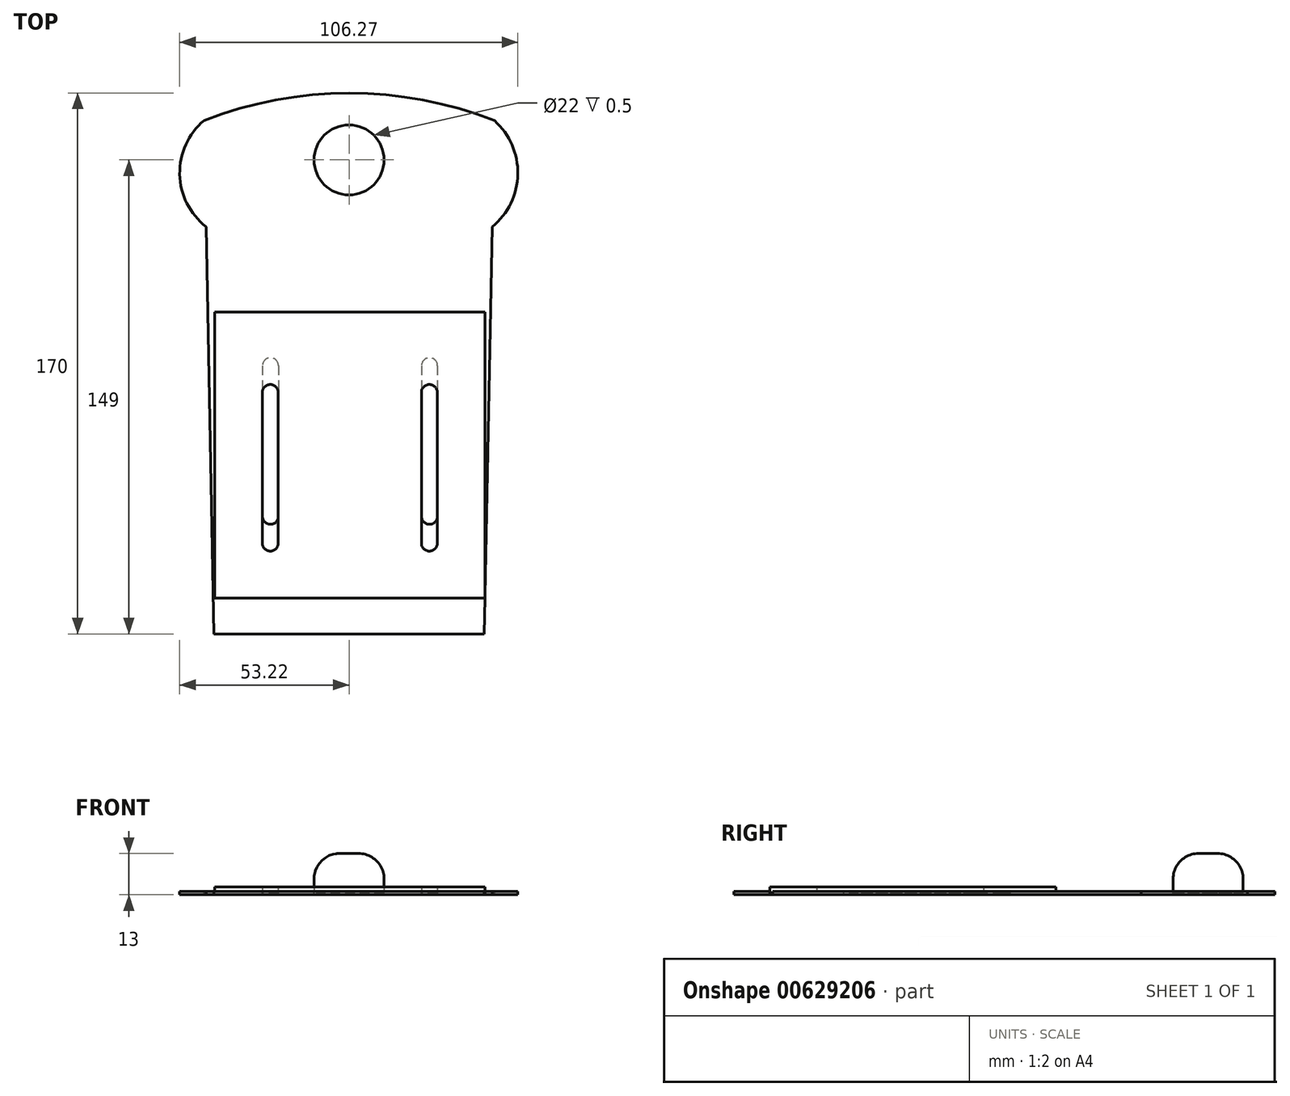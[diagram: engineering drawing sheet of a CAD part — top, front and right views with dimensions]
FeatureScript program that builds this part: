
annotation { "Feature Type Name" : "Feature", "Feature Type Description" : "" }
export const myFeature = defineFeature(function(context is Context, id is Id, definition is map)
    precondition{}
    {
        {
            var Q0;
            Q0=qCreatedBy(makeId("Top.planeOp"),FACE);
            var sketch = newSketch(context, id + "F0", { "sketchPlane" : qUnion([Q0])});
            skCircle(sketch, "E0", {"center": v(0, 0) * mm, "radius": 125 * mm});
            skCircle(sketch, "E1", {"center": v(0, 104) * mm, "radius": 11 * mm});
            skLineSegment(sketch, "E2", {"start": v(-45.58, 116.4) * mm, "end": v(-42.5, -45) * mm});
            skLineSegment(sketch, "E3", {"start": v(-42.5, -45) * mm, "end": v(42.5, -45) * mm});
            skLineSegment(sketch, "E4", {"start": v(45.72, 116.34) * mm, "end": v(42.5, -45) * mm});
            skLineSegment(sketch, "E5", {"start": v(0, 104) * mm, "end": v(0, 115) * mm});
            skLineSegment(sketch, "E6", {"start": v(-44.94, 83) * mm, "end": v(45.06, 83) * mm});
            skCircle(sketch, "E7", {"center": v(-31.72, 99.95) * mm, "radius": 21.5 * mm});
            skCircle(sketch, "E8", {"center": v(31.07, 99.95) * mm, "radius": 21.98 * mm});
            skLineSegment(sketch, "E9.bottom", {"start": v(-42.2, -34.93) * mm, "end": v(42.8, -34.93) * mm});
            skLineSegment(sketch, "E9.top", {"start": v(-42.2, 55.07) * mm, "end": v(42.8, 55.07) * mm});
            skLineSegment(sketch, "E9.left", {"start": v(-42.2, -34.93) * mm, "end": v(-42.2, 55.07) * mm});
            skLineSegment(sketch, "E9.right", {"start": v(42.8, -34.93) * mm, "end": v(42.8, 55.07) * mm});
            skLineSegment(sketch, "E10", {"start": v(-22.2, 39.32) * mm, "end": v(-22.2, -8.05) * mm});
            skLineSegment(sketch, "E11", {"start": v(22.8, 39.32) * mm, "end": v(22.8, -8.05) * mm});
            skLineSegment(sketch, "E12", {"start": v(-27.2, 39.32) * mm, "end": v(-27.2, -8.05) * mm});
            skLineSegment(sketch, "E13", {"start": v(27.8, 39.32) * mm, "end": v(27.8, -8.05) * mm});
            skCircle(sketch, "E14", {"center": v(-24.7, 39.32) * mm, "radius": 2.5 * mm});
            skCircle(sketch, "E15", {"center": v(-24.7, -8.05) * mm, "radius": 2.5 * mm});
            skCircle(sketch, "E16", {"center": v(25.3, -8.05) * mm, "radius": 2.5 * mm});
            skCircle(sketch, "E17", {"center": v(25.3, 39.32) * mm, "radius": 2.5 * mm});
            skSolve(sketch);
        }
        {
            var Q0;
            Q0=makeQuery(id+"F0.imprint","IMPRINT",FACE,{"disambiguationData":[TD([[makeQuery(id+"F0.imprint","IMPRINT",EDGE,{"derivedFrom":sQuery(id+"F0.wireOp",EDGE,"E1")}),1.0]])]});
            var Q1;
            {var subQ0=sQuery(id+"F0.wireOp",EDGE,"E8");var subQ1=sQuery(id+"F0.wireOp",EDGE,"E1");var subQ2=makeQuery(id+"F0.imprint","INTERSECT",VERTEX,{"disambiguationData":[OD(0.0)],"derivedFrom":[subQ1,subQ0]});Q1=makeQuery(id+"F0.imprint","IMPRINT",FACE,{"disambiguationData":[TD([[makeQuery(id+"F0.imprint","IMPRINT",EDGE,{"disambiguationData":[TD([[subQ2,1.0]])],"derivedFrom":subQ1}),1.0]])]});}
            var Q2;
            {var subQ0=sQuery(id+"F0.wireOp",EDGE,"E7");var subQ1=sQuery(id+"F0.wireOp",EDGE,"E1");var subQ2=makeQuery(id+"F0.imprint","INTERSECT",VERTEX,{"disambiguationData":[OD(0.0)],"derivedFrom":[subQ1,subQ0]});Q2=makeQuery(id+"F0.imprint","IMPRINT",FACE,{"disambiguationData":[TD([[makeQuery(id+"F0.imprint","IMPRINT",EDGE,{"disambiguationData":[TD([[subQ2,-1.0]])],"derivedFrom":subQ1}),1.0]])]});}
            extrude(context, id + "F1", {"entities" : qUnion([Q0, Q1, Q2]), "depth" : 12.5 * mm, "offsetDistance" : 25 * mm});
        }
        {
            var Q0;
            Q0=makeQuery(id+"F1.opExtrude","CAP_EDGE",EDGE,{"disambiguationData":[OSD([sQuery(id+"F0.wireOp",EDGE,"E1")])],"isStart":false});
            fillet(context, id + "F2", {"entities" : qUnion([Q0]), "radius" : 8 * mm, "tangentPropagation" : true, "allowEdgeOverflow" : false});
        }
        {
            var Q0;
            {var subQ0=sQuery(id+"F0.wireOp",EDGE,"E3");Q0=makeQuery(id+"F0.imprint","IMPRINT",FACE,{"disambiguationData":[TD([[makeQuery(id+"F0.imprint","IMPRINT",EDGE,{"derivedFrom":subQ0}),-1.0]])]});}
            var sketch = newSketch(context, id + "F3", { "sketchPlane" : qUnion([Q0])});
            skLineSegment(sketch, "E18.bottom", {"start": v(-42.26, -33.76) * mm, "end": v(42.74, -33.76) * mm});
            skLineSegment(sketch, "E18.top", {"start": v(-42.26, 56.24) * mm, "end": v(42.74, 56.24) * mm});
            skLineSegment(sketch, "E18.left", {"start": v(-42.26, -33.76) * mm, "end": v(-42.26, 56.24) * mm});
            skLineSegment(sketch, "E18.right", {"start": v(42.74, -33.76) * mm, "end": v(42.74, 56.24) * mm});
            skLineSegment(sketch, "E19", {"start": v(-22.26, 30.9) * mm, "end": v(-22.26, -16.47) * mm});
            skLineSegment(sketch, "E20", {"start": v(22.74, 30.9) * mm, "end": v(22.74, -16.47) * mm});
            skLineSegment(sketch, "E21", {"start": v(-27.26, 30.9) * mm, "end": v(-27.26, -16.47) * mm});
            skLineSegment(sketch, "E22", {"start": v(27.74, 30.9) * mm, "end": v(27.74, -16.47) * mm});
            skCircle(sketch, "E23", {"center": v(-24.76, 30.9) * mm, "radius": 2.5 * mm});
            skCircle(sketch, "E24", {"center": v(-24.76, -16.47) * mm, "radius": 2.5 * mm});
            skCircle(sketch, "E25", {"center": v(25.24, -16.47) * mm, "radius": 2.5 * mm});
            skCircle(sketch, "E26", {"center": v(25.24, 30.9) * mm, "radius": 2.5 * mm});
            skSolve(sketch);
        }
        {
            var Q0;
            {var subQ11=sQuery(id+"F3.wireOp",EDGE,"E18.top");Q0=makeQuery(id+"F3.imprint","IMPRINT",FACE,{"disambiguationData":[TD([[makeQuery(id+"F3.imprint","IMPRINT",EDGE,{"derivedFrom":subQ11}),-1.0]])]});}
            extrude(context, id + "F4", {"entities" : qUnion([Q0]), "depth" : 2 * mm, "offsetDistance" : 25 * mm});
        }
        {
            var Q0;
            {var subQ0=sQuery(id+"F0.wireOp",EDGE,"E8");var subQ7=sQuery(id+"F0.wireOp",EDGE,"E1");var subQ8=makeQuery(id+"F0.imprint","INTERSECT",VERTEX,{"disambiguationData":[OD(0.0)],"derivedFrom":[subQ7,subQ0]});Q0=makeQuery(id+"F0.imprint","IMPRINT",FACE,{"disambiguationData":[TD([[makeQuery(id+"F0.imprint","IMPRINT",EDGE,{"disambiguationData":[TD([[subQ8,1.0]])],"derivedFrom":subQ7}),-1.0]])]});}
            var Q1;
            {var subQ0=sQuery(id+"F0.wireOp",EDGE,"E8");var subQ1=sQuery(id+"F0.wireOp",EDGE,"E4");var subQ2=makeQuery(id+"F0.imprint","INTERSECT",VERTEX,{"derivedFrom":[sQuery(id+"F0.wireOp",EDGE,"E0"),subQ1,subQ0]});Q1=makeQuery(id+"F0.imprint","IMPRINT",FACE,{"disambiguationData":[TD([[makeQuery(id+"F0.imprint","IMPRINT",EDGE,{"disambiguationData":[TD([[subQ2,-1.0]])],"derivedFrom":subQ1}),1.0]])]});}
            var Q2;
            {var subQ0=sQuery(id+"F0.wireOp",EDGE,"E8");var subQ1=sQuery(id+"F0.wireOp",EDGE,"E6");var subQ3=makeQuery(id+"F0.imprint","INTERSECT",VERTEX,{"derivedFrom":[subQ1,subQ0]});Q2=makeQuery(id+"F0.imprint","IMPRINT",FACE,{"disambiguationData":[TD([[makeQuery(id+"F0.imprint","IMPRINT",EDGE,{"disambiguationData":[TD([[subQ3,-1.0]])],"derivedFrom":subQ1}),-1.0]])]});}
            var Q3;
            {var subQ0=sQuery(id+"F0.wireOp",EDGE,"E7");var subQ7=sQuery(id+"F0.wireOp",EDGE,"E1");var subQ8=makeQuery(id+"F0.imprint","INTERSECT",VERTEX,{"disambiguationData":[OD(0.0)],"derivedFrom":[subQ7,subQ0]});Q3=makeQuery(id+"F0.imprint","IMPRINT",FACE,{"disambiguationData":[TD([[makeQuery(id+"F0.imprint","IMPRINT",EDGE,{"disambiguationData":[TD([[subQ8,-1.0]])],"derivedFrom":subQ7}),-1.0]])]});}
            var Q4;
            {var subQ0=sQuery(id+"F0.wireOp",EDGE,"E7");var subQ1=sQuery(id+"F0.wireOp",EDGE,"E2");var subQ2=makeQuery(id+"F0.imprint","INTERSECT",VERTEX,{"derivedFrom":[sQuery(id+"F0.wireOp",EDGE,"E0"),subQ1,subQ0]});Q4=makeQuery(id+"F0.imprint","IMPRINT",FACE,{"disambiguationData":[TD([[makeQuery(id+"F0.imprint","IMPRINT",EDGE,{"disambiguationData":[TD([[subQ2,-1.0]])],"derivedFrom":subQ1}),-1.0]])]});}
            var Q5;
            {var subQ0=sQuery(id+"F0.wireOp",EDGE,"E7");var subQ1=sQuery(id+"F0.wireOp",EDGE,"E6");var subQ3=makeQuery(id+"F0.imprint","INTERSECT",VERTEX,{"derivedFrom":[subQ1,subQ0]});Q5=makeQuery(id+"F0.imprint","IMPRINT",FACE,{"disambiguationData":[TD([[makeQuery(id+"F0.imprint","IMPRINT",EDGE,{"disambiguationData":[TD([[subQ3,1.0]])],"derivedFrom":subQ1}),-1.0]])]});}
            var Q6;
            {var subQ0=sQuery(id+"F0.wireOp",EDGE,"E7");var subQ1=sQuery(id+"F0.wireOp",EDGE,"E1");var subQ2=makeQuery(id+"F0.imprint","INTERSECT",VERTEX,{"disambiguationData":[OD(1.0)],"derivedFrom":[subQ1,subQ0]});Q6=makeQuery(id+"F0.imprint","IMPRINT",FACE,{"disambiguationData":[TD([[makeQuery(id+"F0.imprint","IMPRINT",EDGE,{"disambiguationData":[TD([[subQ2,-1.0]])],"derivedFrom":subQ1}),-1.0]])]});}
            var Q7;
            {var subQ3=sQuery(id+"F0.wireOp",EDGE,"E1");var subQ5=makeQuery(id+"F0.imprint","IMPRINT",VERTEX,{"derivedFrom":subQ3});Q7=makeQuery(id+"F0.imprint","IMPRINT",FACE,{"disambiguationData":[TD([[makeQuery(id+"F0.imprint","IMPRINT",EDGE,{"disambiguationData":[TD([[subQ5,1.0]])],"derivedFrom":subQ3}),-1.0]])]});}
            var Q8;
            {var subQ1=sQuery(id+"F0.wireOp",EDGE,"E3");Q8=makeQuery(id+"F0.imprint","IMPRINT",FACE,{"disambiguationData":[TD([[makeQuery(id+"F0.imprint","IMPRINT",EDGE,{"derivedFrom":subQ1}),1.0]])]});}
            var Q9;
            {var subQ10=sQuery(id+"F0.wireOp",EDGE,"E9.top");Q9=makeQuery(id+"F0.imprint","IMPRINT",FACE,{"disambiguationData":[TD([[makeQuery(id+"F0.imprint","IMPRINT",EDGE,{"derivedFrom":subQ10}),-1.0]])]});}
            extrude(context, id + "F5", {"entities" : qUnion([Q0, Q1, Q2, Q3, Q4, Q5, Q6, Q7, Q8, Q9]), "operationType" : NewBodyOperationType.ADD, "endBound" : BoundingType.SYMMETRIC, "oppositeDirection" : true, "depth" : 1 * mm, "offsetDistance" : 25 * mm});
        }
    });
